# Revit family: IS_CerathermT125_A7587_BIM_NL
name_source: partatom
category: Plumbing Fixtures
units: mm (PartAtom-declared; Revit-internal decimal feet)

## family parameters
Always vertical = No
Cut with Voids When Loaded = No
OmniClass Number = 23.45.55.17
OmniClass Title = Mixing Faucets
Part Type = Normal
Room Calculation Point = No
Round Connector Dimension = Use Diameter
Shared = No
Work Plane-Based = No

## types (4) — shared parameters
Accesoires = https://www.idealstandard.nl
Accessories = https://www.idealstandard.de
Afmetingen = 303 x 107 x 70 mm
AfstandsEenheid = Millimeter
AreaUnits = millimeters
AssetType = Plumbing Fittures
Auteur = Ideal Standard
BIMObjectName = IS_IdealStandard_ShowermixersCeratherm T125  A7587
BIMobject category = Taps & Mixers
BIMobject category code = sanitary-taps-mixers
BIMobject main category = Sanitary
BIMobject main category code = sanitary
Beschrijvinggarantie = Herstellergarantie
BimObjectNaam = IS_IdealStandard_ShowermixersCeratherm T125  A7587
Brand = Ideal Standard
Brand url = http://www.idealstandard.nl
Category = Plumbing Fixtures
Classification = Shower Mixers
ConnectionType = Plumbing
CurrencyUnit = €
CurrentRevision = 1
Date of publishing = 14/04/2022
Douchebak = No
DurationUnit = Years
DuurEenheid = bar
Edition number = 1
FaucetFunction = Manual Shower Mixer
FaucetOperation = Manual Shower Mixers
FaucetTopDescription = Manual Shower Mixer
Functiekraanwerk = Duschmischer
GTIN code = https://4015413351713
Garantieunits = Jahre
GemaaktOp = 14/04/2022
Help = https://www.idealstandard.ee
Hoogte = 70.04898
Hulp = https://www.idealstandard.ee
IFC Classification = Sanitary Terminal
IfcExportAs = IfcValveType
IfcExportType = FAUCET
Installatieinstructies = https://www.idealstandard.nl
Installation instructions = https://www.idealstandard.nl
InstallationInstructions = https://www.idealstandard.nl
Lengte = 107 mm
LinearUnits = millimeters
MaintenanceInformation = https://www.idealstandard.nl
Manufacturer = Ideal Standard
Manufacturer name = Ideal Standard
ManufacturerURL = http://www.idealstandard.nl
Materiaal = Messing
Material = Messing
Material main = Messing
Merk = Ideal Standard
NBS Reference Code = 45-35-70/335
NBS Reference Description = Shower mixers
Name = ShowermixersCeratherm T125 A7587_IdealStandard
NettWeight = 2.1
Nettogewicht = 2.1
NominalDepth = 107 mm
NominalHeight = 70 mm
NominalLength = 107 mm
NominalWidth = 303 mm
Normen = ShowermixersCeratherm T125 A7587_IdealStandard
OppervlakteEenheid = Millimeter
Product Guid = b272a816-6746-46a6-8b51-f7af0783a5ec
Product SKU = A7587
Product certification = https://www.idealstandard.de
Product data url = https://bimobject.com
Product family = CERATHERM
Product group = Taps & Mixers
Product name = CERATHERM T125 EXPOSED SHOWER MIXER
Product url = https://www.idealstandard.nl
ProductInformation = https://www.idealstandard.nl
ProductSoort = Duschmischer
Productinformatie = https://www.idealstandard.nl
QR code = http://bimobject.com
Revisie = 1
Shape = cylindrical
ShowerType = Shower Mixer
Size = 303 x 107 x 70 mm
Space = internal
SpareParts = https://www.idealstandard.nl
Technical description = https://www.idealstandard.nl
Telefoonnummer = 077 355 08 08
TestPressure = 10 bar
Testdruk = 10 bar
Typeconnectie = Installation
Typekraanwerk = Duschmischer
UNSPSC Code = 301815
URL = http://www.idealstandard.nl
Uniclass 1.4 Code = L725111
Uniclass 1.4 Description = Mixer Taps
Uniclass 2.0 Code = PR-35-06-82
Uniclass 2.0 Description = Shower Mixers
Uniclass 2015 Code = Pr_40_20_87_78
Uniclass 2015 Name = Shower manual water supply sets
Uniclass2015Beschrijving = Shower manual water supply sets
Uniclass2015Code = Pr_40_20_87_78
Uniclass2015Referentie = Pr_40_20_87_78
Uniclass2015Title = Shower manual water supply sets
Uniclass2015Version = v1.25
Uniformat II Code = C1030
Uniformat II Description = Fittings
Urlproducent = https://www.idealstandard.nl
ValutaEenheid = Euro
Versie = 1
Version = 1
VolumeUnits = Litres
Volumeunits = Liter
Vorm = zylindrisch
WRASURL = https://www.wrasapprovals.co.uk
WarrantyDescription = Manufacturer warranty
WarrantyDurationParts = 5
WarrantyDurationUnit = years
Wisselstukken = https://www.idealstandard.nl
Youtube clip = https://www.youtube.com
zero-valued in all types: Breedte, BrutoGewicht, Diepte, MaterialThickness, Vervangingskosten

## per-type parameters (varying)
| type | Afwerking | Artikelnummer | Artikelomschrijving | Artikelreferentie | BarCode | Color | Description | Eigenschappen | Features | Finish | Kleur | MainColor | Model | ModelNumber | ModelReference | Referentie |
| A7587GN - CERATHERM T125 EXPOSED SHOWER MIXER - SILVER STORM | Silberner Sturm | A7587GN | Ceratherm T125 Thermostat-Brauseventil, Stiftgriff mit S-Anschluss - Silver Storm | CERATHERM T125 EXPOSED SHOWER MIXER - SILVER STORM | 4015413352512 | Silver Storm | Ceratherm T125 thermostatic bar shower valve, pin handle with S-Connector - Silver Storm | Thermostatisches Stangen-Duschventil, Stiftgriff mit S-Anschluss - Silver Storm | Thermostatic bar shower valve, pin handle with S-Connector - Silver Storm | Silver Storm | Silberner Sturm | Silver Storm | A7587GN | A7587GN | CERATHERM T125 EXPOSED SHOWER MIXER - SILVER STORM | CERATHERM T125 EXPOSED SHOWER MIXER - SILVER STORM |
| A7587AA - CERATHERM T125 EXPOSED SHOWER MIXER - CHROME | Chrom | A7587AA | Ceratherm T125 Thermostat-Bar-Duschventil, Stiftgriff mit S-Anschluss - Chrom | CERATHERM T125 EXPOSED SHOWER MIXER - CHROME | 4015413351713 | Chrome | Ceratherm T125 thermostatic bar shower valve, pin handle with S-Connector - Chrome | Thermostatisches Stangen-Duschventil, Stiftgriff mit S-Anschluss - Chrom | Thermostatic bar shower valve, pin handle with S-Connector - Chrome | Chrome | Chrom | Chrome | A7587AA | A7587AA | CERATHERM T125 EXPOSED SHOWER MIXER - CHROME | CERATHERM T125 EXPOSED SHOWER MIXER - CHROME |
| A7587A5 - CERATHERM T125 EXPOSED SHOWER MIXER - MAGNETIC GREY | Magnetisches Grau | A7587A5 | Ceratherm T125 Thermostat-Bar-Duschventil, Pin-Griff mit S-Anschluss – Magnetic Grey | CERATHERM T125 EXPOSED SHOWER MIXER - MAGNETIC GREY | 4015413352505 | Magnetic Grey | Ceratherm T125 thermostatic bar shower valve, pin handle with S-Connector - Magnetic Grey | Thermostatisches Stangen-Duschventil, Stiftgriff mit S-Anschluss - Magnetic Grey | Thermostatic bar shower valve, pin handle with S-Connector - Magnetic Grey | Magnetic Grey | Magnetisches Grau | Magnetic Grey | A7587A5 | A7587A5 | CERATHERM T125 EXPOSED SHOWER MIXER - MAGNETIC GREY | CERATHERM T125 EXPOSED SHOWER MIXER - MAGNETIC GREY |
| A7587A2 - CERATHERM T125 EXPOSED SHOWER MIXER - BRUSH GOLD | Pinsel Gold | A7587A2 | Ceratherm T125 Thermostat-Duscharmatur, Stiftgriff mit S-Anschluss - Brush Gold | CERATHERM T125 EXPOSED SHOWER MIXER - BRUSH GOLD | 4015413352499 | Brush Gold | Ceratherm T125 thermostatic bar shower valve, pin handle with S-Connector - Brush Gold | Thermostatisches Stangen-Duschventil, Stiftgriff mit S-Anschluss - Brush Gold | Thermostatic bar shower valve, pin handle with S-Connector - Brush Gold | Brush Gold | Pinsel Gold | Brush Gold | A7587A2 | A7587A2 | CERATHERM T125 EXPOSED SHOWER MIXER - BRUSH GOLD | CERATHERM T125 EXPOSED SHOWER MIXER - BRUSH GOLD |

## geometry (parser evidence)
native form markers: Sweep x4
no freeform markers — native parametric forms only
